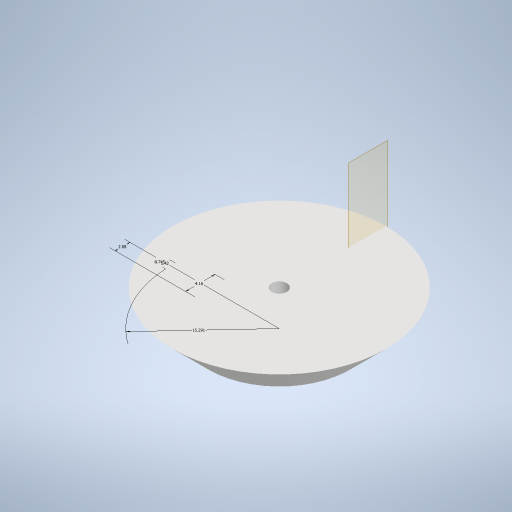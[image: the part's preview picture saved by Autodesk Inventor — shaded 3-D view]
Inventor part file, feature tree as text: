
AUTODESK INVENTOR PART (.ipt)
format: ipt  version: 2023 (Build 270158000, 158)  size: 246,272 bytes
history: native  units: in
note: dims shown in document units (in); Inventor stores cm internally (conversion verified against a paired STEP export)
features: other x1, plane x1, revolve x1, sketch x1
ambient origin geometry x8: Origin, YZ Plane, XZ Plane, XY Plane, X Axis, Y Axis, Z Axis, Center Point
bodies: Body1 (feature_tree)
feature tree (4):
  other  "bevelGear"
  plane  "Work Plane1"
  revolve  "Revolution1"  Angle=360.0deg
  sketch  "Sketch2"  dims[d4=0.1969in d6=360.0deg d10=1.1811in d11=0.1969in d12=0.1969in d13=0.1969in d14=0.1969in d15=0.0423in d16=0.0846in d17=0.1638in d18=0.0819in d21=0.0293in d22=0.0559in d23=0.602in]
